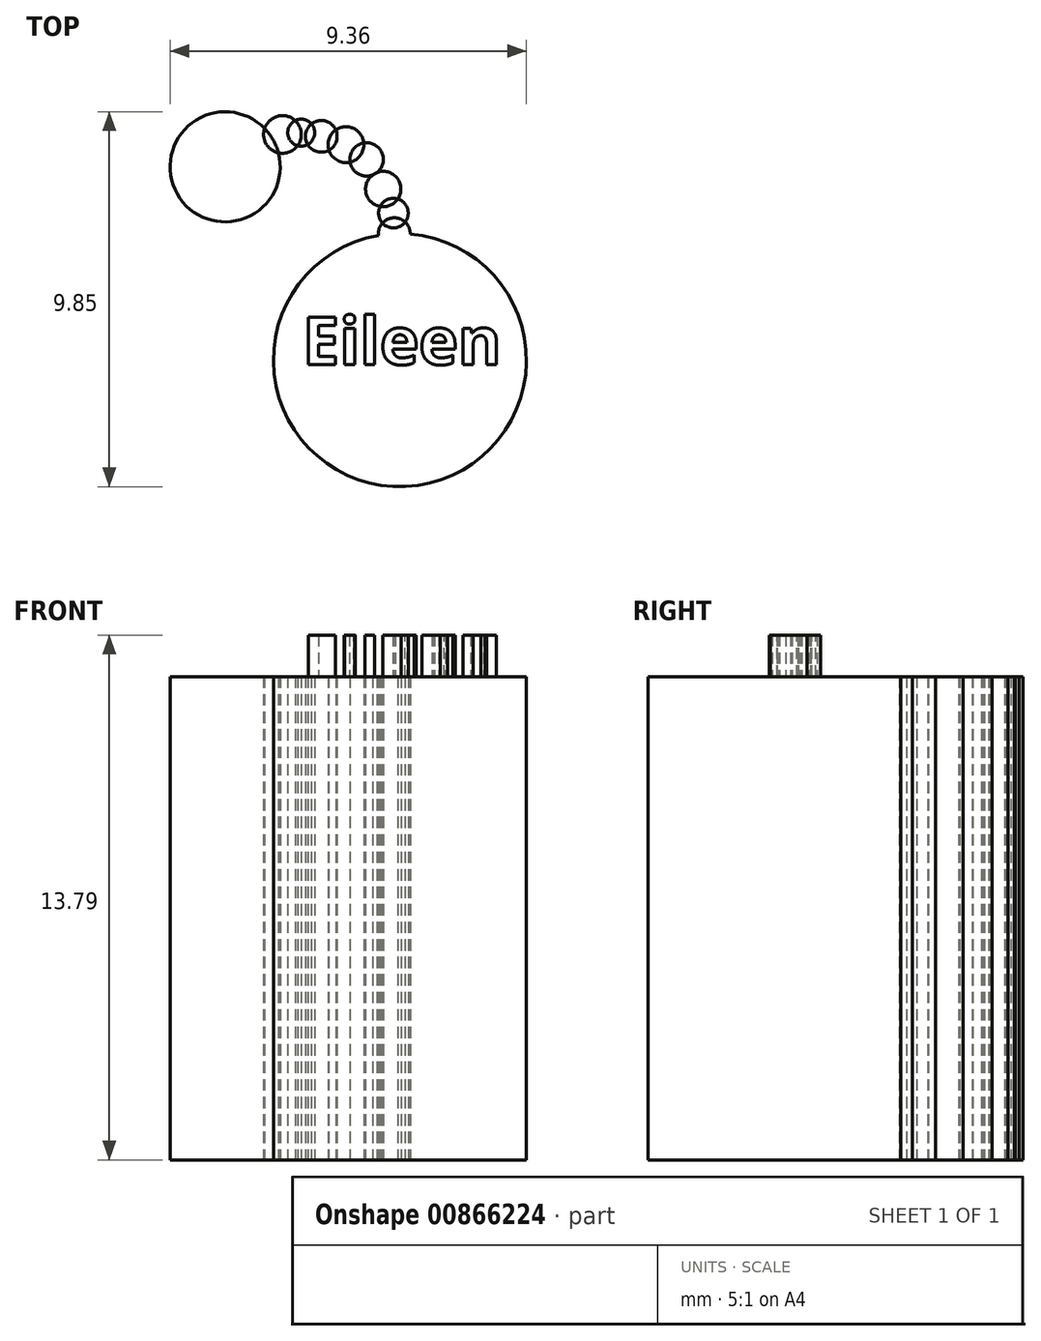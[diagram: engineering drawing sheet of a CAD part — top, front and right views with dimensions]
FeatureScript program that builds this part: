
annotation { "Feature Type Name" : "Feature", "Feature Type Description" : "" }
export const myFeature = defineFeature(function(context is Context, id is Id, definition is map)
    precondition{}
    {
        {
            var Q0;
            Q0=qCreatedBy(makeId("Top.planeOp"),FACE);
            var sketch = newSketch(context, id + "F0", { "sketchPlane" : qUnion([Q0])});
            skCircle(sketch, "E0", {"center": v(1.42, 10.45) * mm, "radius": 3.33 * mm});
            skLineSegment(sketch, "E1", {"start": v(-0.6, 10.74) * mm, "end": v(-0.6, 9.81) * mm});
            skLineSegment(sketch, "E2", {"start": v(0, 11.13) * mm, "end": v(0.23, 10.9) * mm});
            skLineSegment(sketch, "E3", {"start": v(0, 9.81) * mm, "end": v(0, 10.1) * mm});
            skLineSegment(sketch, "E4", {"start": v(-0.6, 10.1) * mm, "end": v(-0.6, 10.28) * mm});
            skCircle(sketch, "E5", {"center": v(-3.18, 15.53) * mm, "radius": 1.45 * mm});
            skCircle(sketch, "E6", {"center": v(-1.67, 16.38) * mm, "radius": 0.5 * mm});
            skCircle(sketch, "E7", {"center": v(-1.18, 16.42) * mm, "radius": 0.35 * mm});
            skCircle(sketch, "E8", {"center": v(-0.65, 16.33) * mm, "radius": 0.42 * mm});
            skCircle(sketch, "E9", {"center": v(0, 16.1) * mm, "radius": 0.47 * mm});
            skCircle(sketch, "E10", {"center": v(0.54, 15.72) * mm, "radius": 0.44 * mm});
            skCircle(sketch, "E11", {"center": v(0.98, 14.94) * mm, "radius": 0.46 * mm});
            skCircle(sketch, "E12", {"center": v(1.25, 14.31) * mm, "radius": 0.39 * mm});
            skCircle(sketch, "E13", {"center": v(1.27, 13.77) * mm, "radius": 0.42 * mm});
            skSolve(sketch);
        }
        {
            var Q0;
            {var subQ0=sQuery(id+"F0.wireOp",EDGE,"E13");var subQ1=sQuery(id+"F0.wireOp",EDGE,"E0");var subQ2=makeQuery(id+"F0.imprint","INTERSECT",VERTEX,{"disambiguationData":[OD(0.0)],"derivedFrom":[subQ1,subQ0]});Q0=makeQuery(id+"F0.imprint","IMPRINT",FACE,{"disambiguationData":[TD([[makeQuery(id+"F0.imprint","IMPRINT",EDGE,{"disambiguationData":[TD([[subQ2,-1.0]])],"derivedFrom":subQ1}),1.0]])]});}
            var Q1;
            {var subQ0=sQuery(id+"F0.wireOp",EDGE,"E6");var subQ1=sQuery(id+"F0.wireOp",EDGE,"E5");var subQ2=makeQuery(id+"F0.imprint","INTERSECT",VERTEX,{"disambiguationData":[OD(0.0)],"derivedFrom":[subQ1,subQ0]});Q1=makeQuery(id+"F0.imprint","IMPRINT",FACE,{"disambiguationData":[TD([[makeQuery(id+"F0.imprint","IMPRINT",EDGE,{"disambiguationData":[TD([[subQ2,-1.0]])],"derivedFrom":subQ1}),1.0]])]});}
            var Q2;
            {var subQ0=sQuery(id+"F0.wireOp",EDGE,"E6");var subQ1=sQuery(id+"F0.wireOp",EDGE,"E5");var subQ2=makeQuery(id+"F0.imprint","INTERSECT",VERTEX,{"disambiguationData":[OD(0.0)],"derivedFrom":[subQ1,subQ0]});Q2=makeQuery(id+"F0.imprint","IMPRINT",FACE,{"disambiguationData":[TD([[makeQuery(id+"F0.imprint","IMPRINT",EDGE,{"disambiguationData":[TD([[subQ2,1.0]])],"derivedFrom":subQ1}),-1.0]])]});}
            var Q3;
            {var subQ0=sQuery(id+"F0.wireOp",EDGE,"E7");var subQ1=sQuery(id+"F0.wireOp",EDGE,"E6");var subQ2=makeQuery(id+"F0.imprint","INTERSECT",VERTEX,{"disambiguationData":[OD(0.0)],"derivedFrom":[subQ1,subQ0]});Q3=makeQuery(id+"F0.imprint","IMPRINT",FACE,{"disambiguationData":[TD([[makeQuery(id+"F0.imprint","IMPRINT",EDGE,{"disambiguationData":[TD([[subQ2,1.0]])],"derivedFrom":subQ1}),-1.0]])]});}
            var Q4;
            {var subQ0=sQuery(id+"F0.wireOp",EDGE,"E8");var subQ1=sQuery(id+"F0.wireOp",EDGE,"E7");var subQ2=makeQuery(id+"F0.imprint","INTERSECT",VERTEX,{"disambiguationData":[OD(0.0)],"derivedFrom":[subQ1,subQ0]});Q4=makeQuery(id+"F0.imprint","IMPRINT",FACE,{"disambiguationData":[TD([[makeQuery(id+"F0.imprint","IMPRINT",EDGE,{"disambiguationData":[TD([[subQ2,1.0]])],"derivedFrom":subQ1}),-1.0]])]});}
            var Q5;
            {var subQ0=sQuery(id+"F0.wireOp",EDGE,"E9");var subQ1=sQuery(id+"F0.wireOp",EDGE,"E8");var subQ2=makeQuery(id+"F0.imprint","INTERSECT",VERTEX,{"disambiguationData":[OD(0.0)],"derivedFrom":[subQ1,subQ0]});Q5=makeQuery(id+"F0.imprint","IMPRINT",FACE,{"disambiguationData":[TD([[makeQuery(id+"F0.imprint","IMPRINT",EDGE,{"disambiguationData":[TD([[subQ2,1.0]])],"derivedFrom":subQ1}),-1.0]])]});}
            var Q6;
            {var subQ0=sQuery(id+"F0.wireOp",EDGE,"E10");var subQ1=sQuery(id+"F0.wireOp",EDGE,"E9");var subQ2=makeQuery(id+"F0.imprint","INTERSECT",VERTEX,{"disambiguationData":[OD(0.0)],"derivedFrom":[subQ1,subQ0]});Q6=makeQuery(id+"F0.imprint","IMPRINT",FACE,{"disambiguationData":[TD([[makeQuery(id+"F0.imprint","IMPRINT",EDGE,{"disambiguationData":[TD([[subQ2,1.0]])],"derivedFrom":subQ1}),-1.0]])]});}
            var Q7;
            {var subQ0=sQuery(id+"F0.wireOp",EDGE,"E11");var subQ1=sQuery(id+"F0.wireOp",EDGE,"E10");var subQ2=makeQuery(id+"F0.imprint","INTERSECT",VERTEX,{"disambiguationData":[OD(0.0)],"derivedFrom":[subQ1,subQ0]});Q7=makeQuery(id+"F0.imprint","IMPRINT",FACE,{"disambiguationData":[TD([[makeQuery(id+"F0.imprint","IMPRINT",EDGE,{"disambiguationData":[TD([[subQ2,-1.0]])],"derivedFrom":subQ1}),-1.0]])]});}
            var Q8;
            {var subQ0=sQuery(id+"F0.wireOp",EDGE,"E13");var subQ1=sQuery(id+"F0.wireOp",EDGE,"E0");var subQ2=makeQuery(id+"F0.imprint","INTERSECT",VERTEX,{"disambiguationData":[OD(0.0)],"derivedFrom":[subQ1,subQ0]});Q8=makeQuery(id+"F0.imprint","IMPRINT",FACE,{"disambiguationData":[TD([[makeQuery(id+"F0.imprint","IMPRINT",EDGE,{"disambiguationData":[TD([[subQ2,1.0]])],"derivedFrom":subQ1}),1.0]])]});}
            var Q9;
            {var subQ0=sQuery(id+"F0.wireOp",EDGE,"E12");var subQ1=sQuery(id+"F0.wireOp",EDGE,"E11");var subQ2=makeQuery(id+"F0.imprint","INTERSECT",VERTEX,{"disambiguationData":[OD(0.0)],"derivedFrom":[subQ1,subQ0]});Q9=makeQuery(id+"F0.imprint","IMPRINT",FACE,{"disambiguationData":[TD([[makeQuery(id+"F0.imprint","IMPRINT",EDGE,{"disambiguationData":[TD([[subQ2,-1.0]])],"derivedFrom":subQ1}),-1.0]])]});}
            var Q10;
            {var subQ0=sQuery(id+"F0.wireOp",EDGE,"E13");var subQ1=sQuery(id+"F0.wireOp",EDGE,"E0");var subQ2=makeQuery(id+"F0.imprint","INTERSECT",VERTEX,{"disambiguationData":[OD(0.0)],"derivedFrom":[subQ1,subQ0]});Q10=makeQuery(id+"F0.imprint","IMPRINT",FACE,{"disambiguationData":[TD([[makeQuery(id+"F0.imprint","IMPRINT",EDGE,{"disambiguationData":[TD([[subQ2,1.0]])],"derivedFrom":subQ1}),-1.0]])]});}
            extrude(context, id + "F1", {"entities" : qUnion([Q0, Q1, Q2, Q3, Q4, Q5, Q6, Q7, Q8, Q9, Q10]), "depth" : 12.7 * mm, "offsetDistance" : 25.4 * mm});
        }
        {
            var Q0;
            Q0=makeQuery(id+"F1.opExtrude","CAP_FACE",FACE,{"disambiguationData":[OSD([sQuery(id+"F0.wireOp",EDGE,"E0"),sQuery(id+"F0.wireOp",EDGE,"E12"),sQuery(id+"F0.wireOp",EDGE,"E13")])],"isStart":false});
            var sketch = newSketch(context, id + "F2", { "sketchPlane" : qUnion([Q0])});
            skText(sketch, "E14", { "text": "Eileen", "fontName": "OpenSans-Bold.ttf"});
            const initialGuessF2  = {"E14": [-0.00114, 0.01033, 1, 0, 0.00125]};
            skSetInitialGuess(sketch, initialGuessF2);
            skSolve(sketch);
        }
        {
            var Q0;
            Q0 = qSketchRegion(id + "F2", true);
            extrude(context, id + "F3", {"entities" : qUnion([Q0]), "operationType" : NewBodyOperationType.ADD, "depth" : 1.1 * mm, "offsetDistance" : 25.4 * mm});
        }
    });
